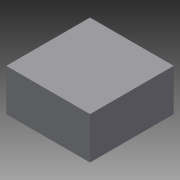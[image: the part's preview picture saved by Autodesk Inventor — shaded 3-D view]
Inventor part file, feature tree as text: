
AUTODESK INVENTOR PART (.ipt)
format: ipt  version: 2015 (Build 190159000, 159)  size: 68,608 bytes
history: native  units: in
note: dims shown in document units (in); Inventor stores cm internally (conversion verified against a paired STEP export)
features: extrude x1, sketch x1
ambient origin geometry x8: Origin, YZ Plane, XZ Plane, XY Plane, X Axis, Y Axis, Z Axis, Center Point
bodies: Solid1 (feature_tree)
feature tree (2):
  extrude  "Extrusion1"  Depth=2.2835in
  sketch  "Sketch1"  dims[d0=2.2835in d1=2.2835in d2=1.1417in d3=0.0in]
